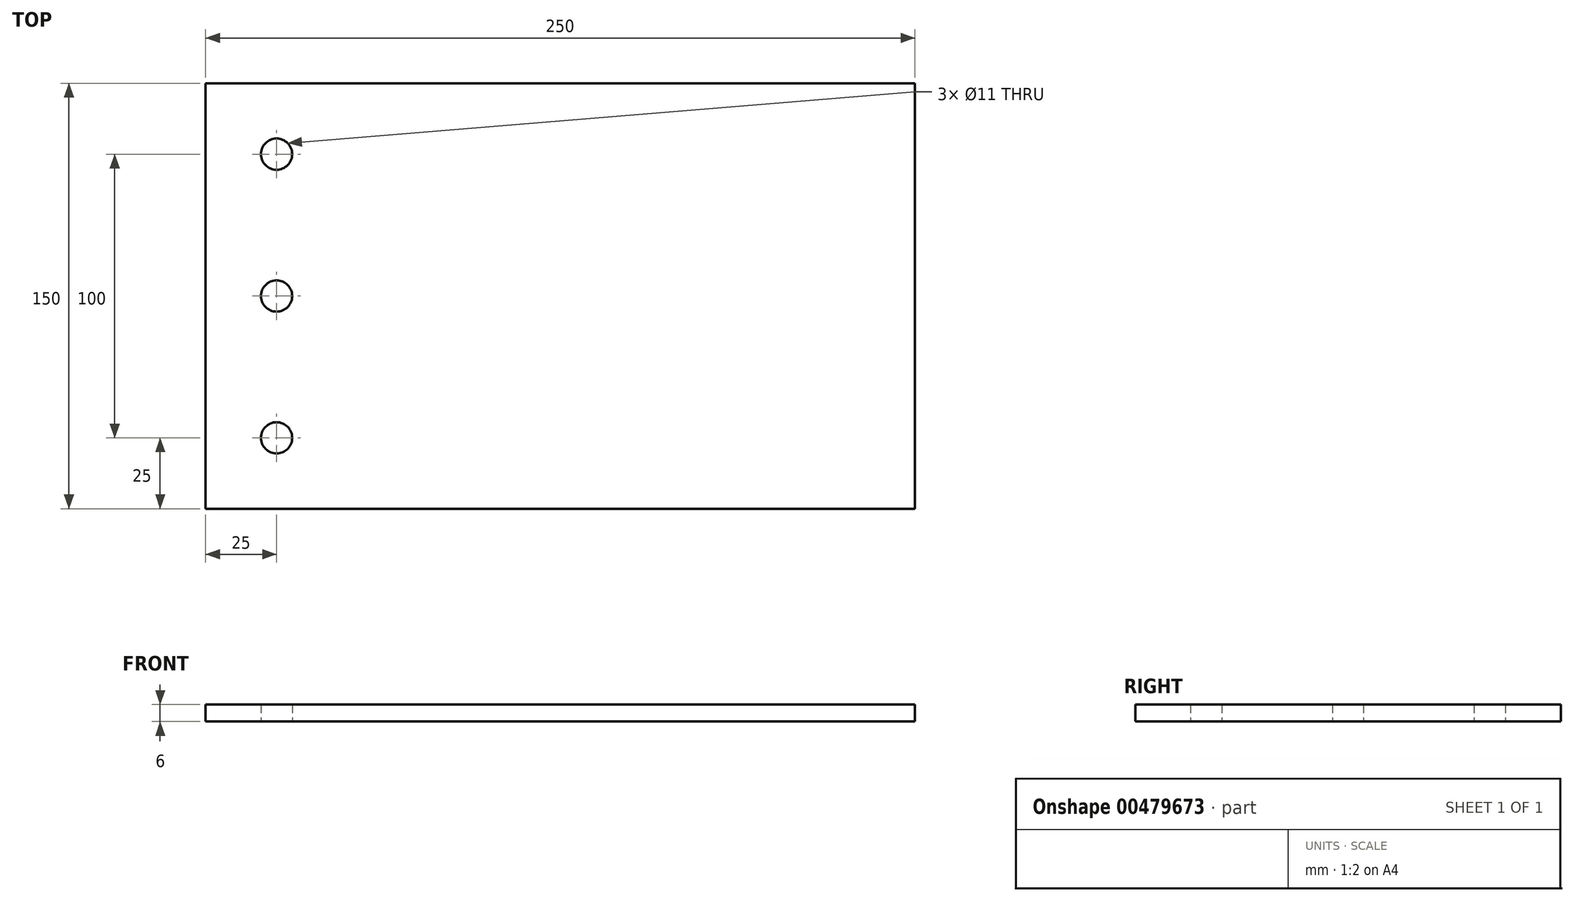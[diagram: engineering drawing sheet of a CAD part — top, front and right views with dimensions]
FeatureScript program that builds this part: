
annotation { "Feature Type Name" : "Feature", "Feature Type Description" : "" }
export const myFeature = defineFeature(function(context is Context, id is Id, definition is map)
    precondition{}
    {
        {
            var Q0;
            Q0=qCreatedBy(makeId("Top.planeOp"),FACE);
            var sketch = newSketch(context, id + "F0", { "sketchPlane" : qUnion([Q0])});
            skLineSegment(sketch, "E0.bottom", {"start": v(125, -75) * mm, "end": v(-125, -75) * mm});
            skLineSegment(sketch, "E0.top", {"start": v(125, 75) * mm, "end": v(-125, 75) * mm});
            skLineSegment(sketch, "E0.left", {"start": v(125, -75) * mm, "end": v(125, 75) * mm});
            skLineSegment(sketch, "E0.right", {"start": v(-125, -75) * mm, "end": v(-125, 75) * mm});
            skPoint(sketch, "E0.middle", {"position": v(0, 0) * mm});
            skPoint(sketch, "E1", {"position": v(-100, 50) * mm});
            skPoint(sketch, "E2", {"position": v(-100, 0) * mm});
            skPoint(sketch, "E3", {"position": v(-100, -50) * mm});
            skSolve(sketch);
        }
        {
            var Q0;
            Q0 = qSketchRegion(id + "F0", true);
            extrude(context, id + "F1", {"entities" : qUnion([Q0]), "depth" : 6 * mm, "offsetDistance" : 25 * mm});
        }
        {
            var Q0;
            Q0=sQuery(id+"F0.wireOp",VERTEX,"E1");
            var Q1;
            Q1=sQuery(id+"F0.wireOp",VERTEX,"E2");
            var Q2;
            Q2=sQuery(id+"F0.wireOp",VERTEX,"E3");
            var Q3;
            Q3=makeQuery(id+"F1.opExtrude","SWEPT_BODY",BODY,{"disambiguationData":[OSD([sQuery(id+"F0.wireOp",EDGE,"E0.bottom"),sQuery(id+"F0.wireOp",EDGE,"E0.top"),sQuery(id+"F0.wireOp",EDGE,"E0.left"),sQuery(id+"F0.wireOp",EDGE,"E0.right")])]});
            hole(context, id + "F2", {"style" : HoleStyle.SIMPLE, "endStyle" : HoleEndStyle.BLIND, "oppositeDirection" : true, "holeDiameter" : 11 * mm, "majorDiameter" : 5 * mm, "holeDepth" : 6 * mm, "isTappedThrough" : true, "tappedDepth" : 12 * mm, "tapClearance" : 3, "locations" : qUnion([Q0, Q1, Q2]), "scope" : qUnion([Q3])});
        }
    });
